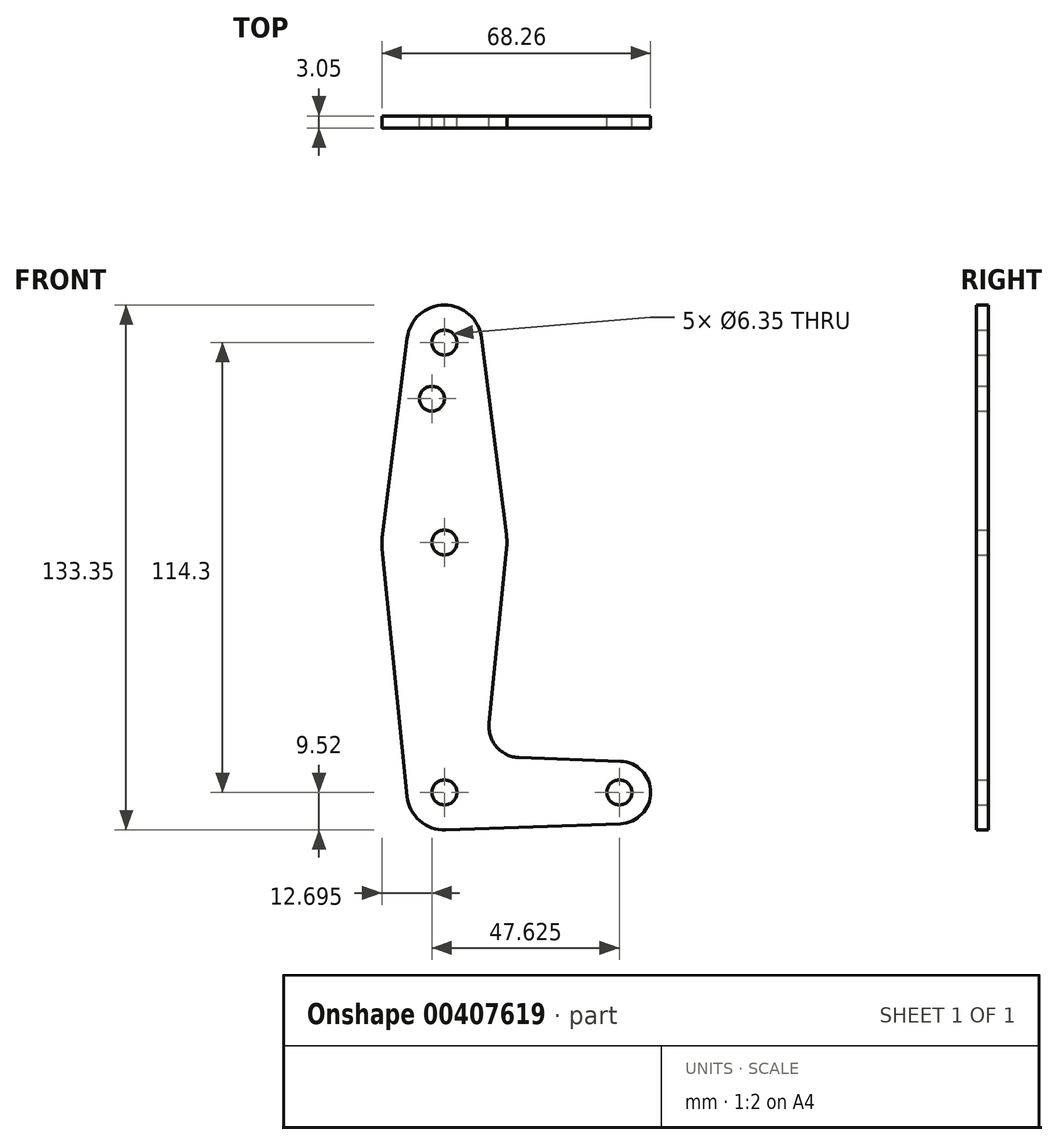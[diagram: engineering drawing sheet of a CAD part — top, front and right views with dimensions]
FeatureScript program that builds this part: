
annotation { "Feature Type Name" : "Feature", "Feature Type Description" : "" }
export const myFeature = defineFeature(function(context is Context, id is Id, definition is map)
    precondition{}
    {
        {
            var Q0;
            Q0=qCreatedBy(makeId("Front.planeOp"),FACE);
            var sketch = newSketch(context, id + "F0", { "sketchPlane" : qUnion([Q0])});
            skCircle(sketch, "E0", {"center": v(0, 0) * mm, "radius": 9.53 * mm});
            skCircle(sketch, "E1", {"center": v(0, 114.3) * mm, "radius": 9.53 * mm});
            skLineSegment(sketch, "E2", {"start": v(0, 0) * mm, "end": v(0, 114.3) * mm, "construction": true});
            skLineSegment(sketch, "E3", {"start": v(0, 0) * mm, "end": v(44.45, 0) * mm, "construction": true});
            skCircle(sketch, "E4", {"center": v(44.45, 0) * mm, "radius": 7.94 * mm});
            skCircle(sketch, "E5", {"center": v(0, 63.5) * mm, "radius": 15.88 * mm});
            skLineSegment(sketch, "E6", {"start": v(9.45, 115.5) * mm, "end": v(15.75, 65.48) * mm});
            skLineSegment(sketch, "E7", {"start": v(-9.45, 115.5) * mm, "end": v(-15.75, 65.48) * mm});
            skLineSegment(sketch, "E8", {"start": v(-15.8, 61.91) * mm, "end": v(-9.48, -0.95) * mm});
            skLineSegment(sketch, "E9", {"start": v(15.8, 61.91) * mm, "end": v(11.34, 17.6) * mm});
            skLineSegment(sketch, "E10", {"start": v(18.97, 8.85) * mm, "end": v(44.73, 7.94) * mm});
            skLineSegment(sketch, "E11", {"start": v(0.34, -9.52) * mm, "end": v(44.73, -7.94) * mm});
            skCircle(sketch, "E12", {"center": v(0, 114.3) * mm, "radius": 3.18 * mm});
            skCircle(sketch, "E13", {"center": v(0, 63.5) * mm, "radius": 3.18 * mm});
            skCircle(sketch, "E14", {"center": v(0, 0) * mm, "radius": 3.18 * mm});
            skCircle(sketch, "E15", {"center": v(44.45, 0) * mm, "radius": 3.18 * mm});
            skCircle(sketch, "E16", {"center": v(-3.18, 100.03) * mm, "radius": 3.18 * mm});
            skArc(sketch, "E17.filletArc", {"start": v(11.34, 17.6) * mm, "mid": v(13.26, 11.57) * mm, "end": v(18.97, 8.85) * mm});
            skSolve(sketch);
        }
        {
            var Q0;
            Q0 = qSketchRegion(id + "F0", true);
            extrude(context, id + "F1", {"entities" : qUnion([Q0]), "depth" : 3.05 * mm});
        }
    });
